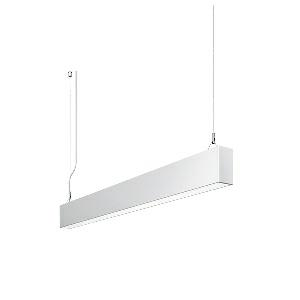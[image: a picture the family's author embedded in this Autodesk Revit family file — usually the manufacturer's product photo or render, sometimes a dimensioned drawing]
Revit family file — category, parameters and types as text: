
# Revit family: dotoo_line_-_dlp_1500_830_d_00805801_0a82
name_source: partatom
category: Lighting Fixtures
units: mm (PartAtom-declared; Revit-internal decimal feet)

## family parameters
Cut with Voids When Loaded = No
Host = Face
Light Source = No
Part Type = Normal
Room Calculation Point = No
Round Connector Dimension = Use Diameter
Shared = No

## types (1)
- DOTOO.line - DLP 1500/830/D (1 x LED, 1300 lm, 3000K)
    Apparent Load = 13 VA
    Approval mark = CE
    CIE Flux Codes = 67 91 98 100 100
    Color Rendering = 80-89
    Color Temperature = 3000K
    Control Gear = Electronic ballast
    Default Elevation = 1800 mm
    Description = DLP 1500/830/D|Suspended luminaire|light source: LED|connected load: 220-240 V, 50/60 Hz|Power consumption: approx. 13 W|standby: approx. 0,20|luminous flux: 1300 lm|luminous efficacy: 100 lm/W|light distribution: Direct|direct ratio: approx. 100 %|colour temperature: Warm white, ca. 3000 K|color rendering index (CRI): >= 80|chromaticity tolerance:  3 SDCM|System of protection: IP 40|technology: Continuously dimmable|luminaire body|material: Sectional aluminium|colour: White|lamp cover: Acrylic (PMMA), Clear|mains lead: 2.00 m With free stranded wires|Fastening: Steel cable 0.3 - 0.7 m|glare control: Prism aperture|luminance(L65): <= 3000 cd/m|unified glare rating(4H 8H): <=  19|special features: DALI Load 1x, TouchDIM - dimming via standard switch, Flicker-free, Suitable as emergency lighting|
    Frequency = 50 Hz
    Height = 110 mm
    Lamp = 1 x LED
    Lamp Light Flux = 1300 lm
    Lamp count = 1
    Length = 1134 mm
    Luminous efficacy = 100 lm/W
    Manufacturer = Waldmann
    ModVariant = No
    Model = 00805801
    Mounting Place = Ceiling
    Mounting Type = Pendant
    Number of Poles = 1
    OnlyDefault = Yes
    Power Factor = 1
    Product Name = DOTOO.line - DLP 1500/830/D
    Product group = Suspended luminaire
    ProductGroupID = 9
    Protection Class = Protection class I
    Protection Degree = IP 40
    RLX_Detail_Level = 1
    RLX_Emergency_Light_Flux = 0 lm
    RLX_Emergency_Type = 0
    RLX_Emergency_Type_DB = No
    RlxData = <blob elided: 19153 chars, md5=bed0e869>
    Socket = socket
    Standby Power = 0 W
    System Light Flux = 1300 lm
    System Power = 13 W
    Type Comments = Product without accessories
    Type Image = 113289000-00692516.jpg
    URL = http://relux.com
    VarID = ---
    Voltage = 230 V
    Voltage Range = 220-240 V
    Weight = 0.00 kg
    Width = 60 mm  [stored 0.19685 ft]

note: [stored X ft] marks values corroborated as IEEE doubles in the binary element streams (Revit-internal decimal feet)

## geometry (parser evidence)
native form markers: Blend x4, Sweep x11
no freeform markers — native parametric forms only
